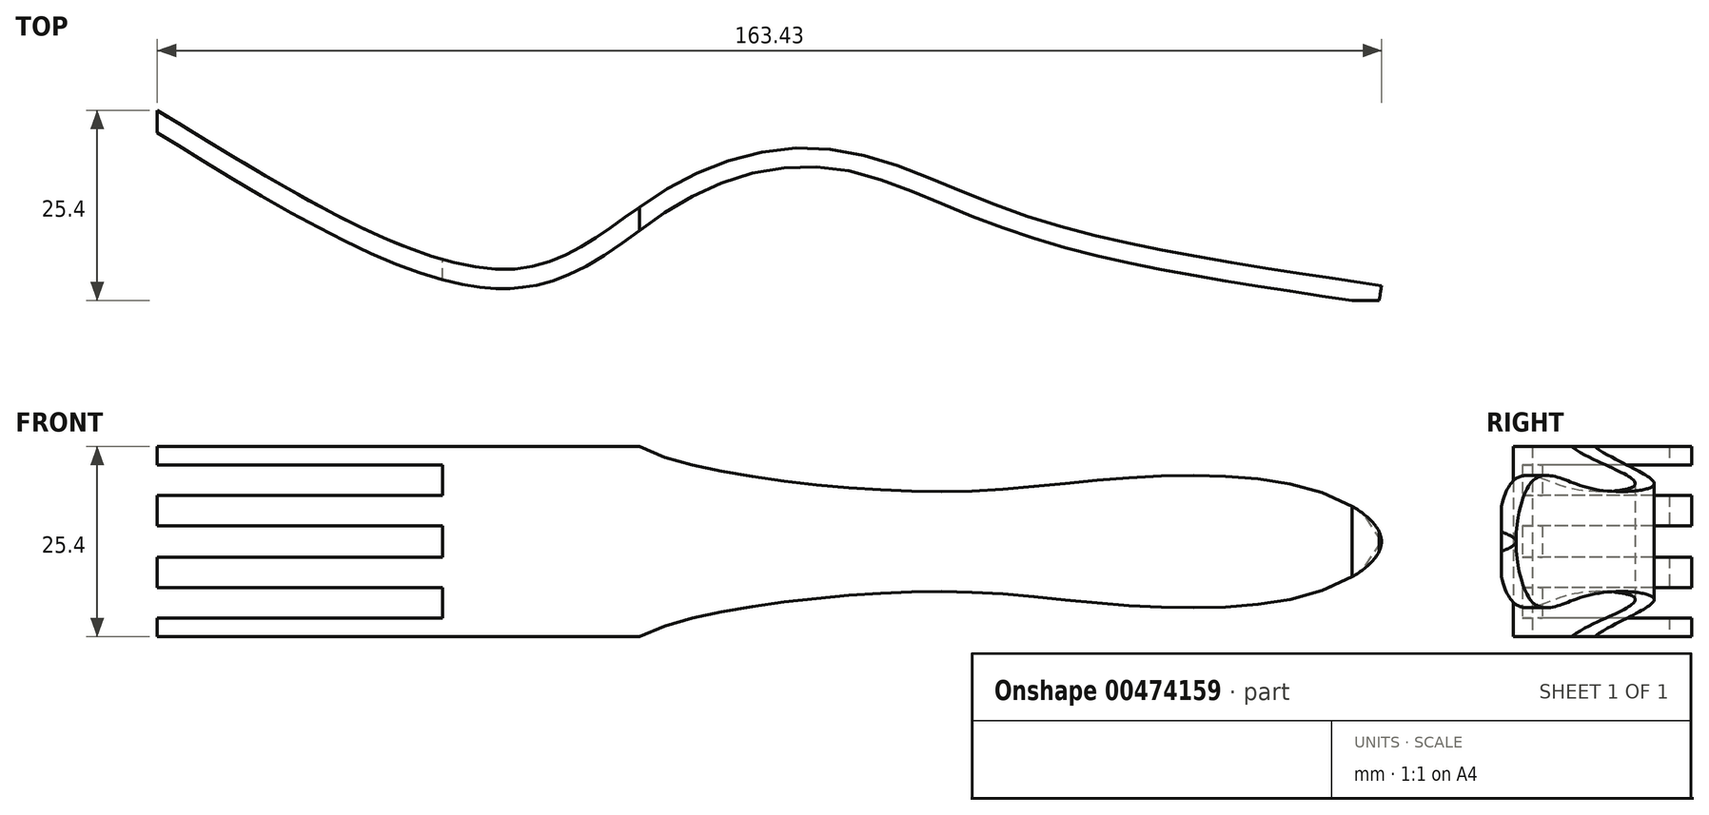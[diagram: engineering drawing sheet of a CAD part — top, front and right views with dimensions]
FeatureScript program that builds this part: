
annotation { "Feature Type Name" : "Feature", "Feature Type Description" : "" }
export const myFeature = defineFeature(function(context is Context, id is Id, definition is map)
    precondition{}
    {
        {
            var Q0;
            Q0=qCreatedBy(makeId("Top.planeOp"),FACE);
            var sketch = newSketch(context, id + "F0", { "sketchPlane" : qUnion([Q0])});
            skFitSpline(sketch, "E0", {"points": [v(0, 0) * mm, v(47.22, -21.22) * mm, v(67.7, -10.71) * mm, v(89.83, -5.18) * mm, v(115.84, -14.03) * mm, v(163.43, -23.44) * mm], "startDerivative": vector(196.55, -120.08) * mm, "endDerivative": vector(214.37, -33.3) * mm});
            skFitSpline(sketch, "E1.0", {"points": [v(-1.32, -2.17) * mm, v(2.76, -4.66) * mm, v(9.14, -8.61) * mm, v(17.73, -13.59) * mm, v(24.12, -17) * mm, v(30.38, -19.94) * mm, v(35.41, -21.83) * mm, v(39.31, -22.92) * mm, v(42.17, -23.5) * mm, v(44.48, -23.75) * mm, v(46.3, -23.8) * mm, v(47.64, -23.76) * mm, v(48.94, -23.63) * mm, v(50.63, -23.36) * mm, v(52.64, -22.83) * mm, v(54.9, -21.97) * mm, v(57.73, -20.57) * mm, v(60.98, -18.5) * mm, v(64, -16.3) * mm, v(66.37, -14.6) * mm, v(68.14, -13.4) * mm, v(69.93, -12.31) * mm, v(71.78, -11.31) * mm, v(73.67, -10.42) * mm, v(76.25, -9.37) * mm, v(79.55, -8.35) * mm, v(82.89, -7.76) * mm, v(85.54, -7.55) * mm, v(87.52, -7.54) * mm, v(89.48, -7.67) * mm, v(92.07, -8.04) * mm, v(95.35, -8.87) * mm, v(99.45, -10.3) * mm, v(103.76, -12.06) * mm, v(108.37, -13.98) * mm, v(112.5, -15.58) * mm, v(116.04, -16.79) * mm, v(119.7, -17.91) * mm, v(124.46, -19.18) * mm, v(130.46, -20.53) * mm, v(136.7, -21.75) * mm, v(143.13, -22.86) * mm, v(151.88, -24.25) * mm, v(158.58, -25.26) * mm, v(163.04, -25.95) * mm]});
            skLineSegment(sketch, "E2", {"start": v(0, 0) * mm, "end": v(-1.32, -2.17) * mm});
            skLineSegment(sketch, "E3", {"start": v(163.43, -23.44) * mm, "end": v(163.04, -25.95) * mm});
            skSolve(sketch);
        }
        {
            var Q0;
            Q0=makeQuery(id+"F0.imprint","IMPRINT",FACE,{"disambiguationData":[TD([[makeQuery(id+"F0.imprint","IMPRINT",EDGE,{"derivedFrom":sQuery(id+"F0.wireOp",EDGE,"E0")}),-1.0]])]});
            extrude(context, id + "F1", {"entities" : qUnion([Q0]), "endBound" : BoundingType.SYMMETRIC, "depth" : 25.4 * mm});
        }
        {
            var Q0;
            Q0=qCreatedBy(makeId("Front.planeOp"),FACE);
            var sketch = newSketch(context, id + "F2", { "sketchPlane" : qUnion([Q0])});
            skLineSegment(sketch, "E4", {"start": v(38.1, 0) * mm, "end": v(38.1, -2.07) * mm});
            skLineSegment(sketch, "E5", {"start": v(38.1, -2.07) * mm, "end": v(0, -2.07) * mm});
            skLineSegment(sketch, "E6", {"start": v(0, -2.07) * mm, "end": v(0, -6.15) * mm});
            skLineSegment(sketch, "E7", {"start": v(0, -6.15) * mm, "end": v(38.1, -6.15) * mm});
            skLineSegment(sketch, "E8", {"start": v(38.1, -6.15) * mm, "end": v(38.1, -10.23) * mm});
            skLineSegment(sketch, "E9", {"start": v(38.1, -10.23) * mm, "end": v(0, -10.23) * mm});
            skLineSegment(sketch, "E10", {"start": v(0, -10.23) * mm, "end": v(0, -13.28) * mm});
            skLineSegment(sketch, "E11", {"start": v(0, -13.28) * mm, "end": v(63.5, -13.28) * mm});
            skFitSpline(sketch, "E12", {"points": [v(63.5, -13.28) * mm, v(100.4, -6.73) * mm, v(127.23, -8.35) * mm, v(155.02, -6.73) * mm, v(163.43, 0) * mm], "startDerivative": vector(42.55, 34.56) * mm, "endDerivative": vector(0, 45.04) * mm});
            skLineSegment(sketch, "E13.MirrorCS", {"start": v(0, 10.23) * mm, "end": v(0, 13.28) * mm});
            skLineSegment(sketch, "E14.MirrorCS", {"start": v(0, 2.07) * mm, "end": v(0, 6.15) * mm});
            skLineSegment(sketch, "E15.MirrorCS", {"start": v(38.1, 6.15) * mm, "end": v(38.1, 10.23) * mm});
            skLineSegment(sketch, "E16.MirrorCS", {"start": v(38.1, 0) * mm, "end": v(38.1, 2.07) * mm});
            skLineSegment(sketch, "E17.MirrorCS", {"start": v(38.1, 10.23) * mm, "end": v(0, 10.23) * mm});
            skFitSpline(sketch, "E18.MirrorCS", {"points": [v(63.5, 13.28) * mm, v(100.4, 6.73) * mm, v(127.23, 8.35) * mm, v(155.02, 6.73) * mm, v(163.43, 0) * mm], "startDerivative": vector(42.55, -34.56) * mm, "endDerivative": vector(0, -45.04) * mm});
            skLineSegment(sketch, "E19.MirrorCS", {"start": v(0, 13.28) * mm, "end": v(63.5, 13.28) * mm});
            skLineSegment(sketch, "E20.MirrorCS", {"start": v(0, 6.15) * mm, "end": v(38.1, 6.15) * mm});
            skLineSegment(sketch, "E21.MirrorCS", {"start": v(38.1, 2.07) * mm, "end": v(0, 2.07) * mm});
            skLineSegment(sketch, "E22", {"start": v(163.43, 0) * mm, "end": v(163.43, 0) * mm});
            skSolve(sketch);
        }
        {
            var Q0;
            Q0=makeQuery(id+"F2.imprint","IMPRINT",FACE,{"disambiguationData":[TD([[makeQuery(id+"F2.imprint","IMPRINT",EDGE,{"derivedFrom":sQuery(id+"F2.wireOp",EDGE,"E4")}),1.0]])]});
            extrude(context, id + "F3", {"entities" : qUnion([Q0]), "operationType" : NewBodyOperationType.INTERSECT, "depth" : 25.4 * mm});
        }
    });
